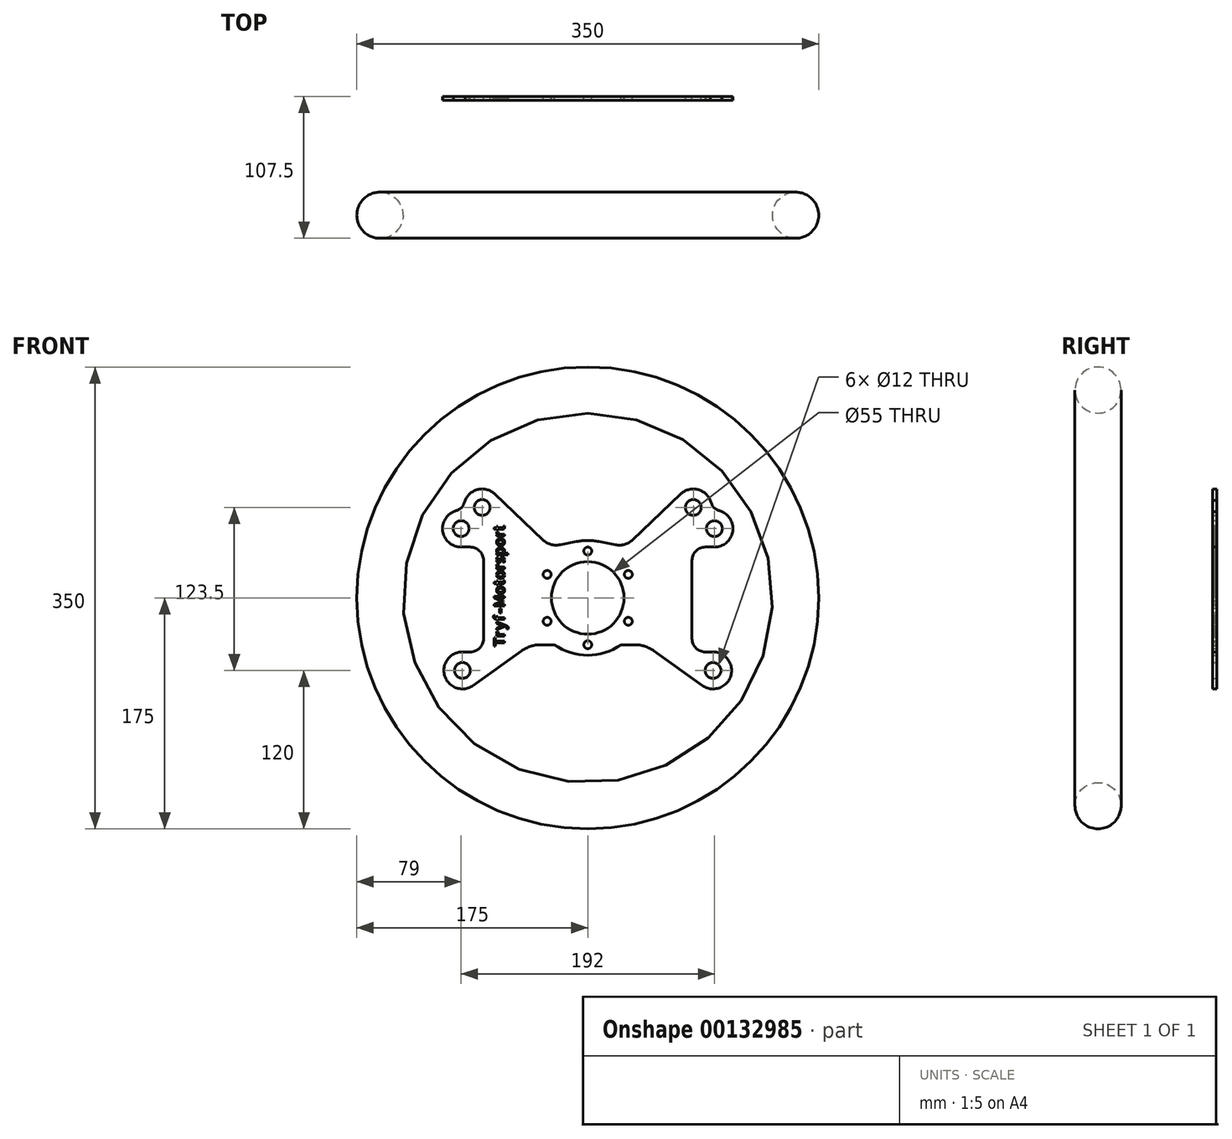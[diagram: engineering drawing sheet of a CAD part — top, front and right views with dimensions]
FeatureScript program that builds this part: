
annotation { "Feature Type Name" : "Feature", "Feature Type Description" : "" }
export const myFeature = defineFeature(function(context is Context, id is Id, definition is map)
    precondition{}
    {
        {
            var Q0;
            Q0=qCreatedBy(makeId("Front.planeOp"),FACE);
            cPlane(context, id + "F0", {"entities" : qUnion([Q0]), "cplaneType" : CPlaneType.OFFSET, "offset" : 90 * mm, "oppositeDirection" : true, "width" : 150 * mm, "height" : 150 * mm});
        }
        {
            var Q0;
            Q0=qCreatedBy(id+"F0.planeOp",FACE);
            var sketch = newSketch(context, id + "F1", { "sketchPlane" : qUnion([Q0])});
            skLineSegment(sketch, "E0", {"start": v(0, 175) * mm, "end": v(0, -175) * mm, "construction": true});
            skLineSegment(sketch, "E1", {"start": v(-175, 0) * mm, "end": v(175, 0) * mm, "construction": true});
            skCircle(sketch, "E2", {"center": v(0, 0) * mm, "radius": 175 * mm, "construction": true});
            skCircle(sketch, "E3", {"center": v(0, 0) * mm, "radius": 27.5 * mm});
            skCircle(sketch, "E4", {"center": v(0, 35.5) * mm, "radius": 3 * mm});
            skCircle(sketch, "E5.1.0", {"center": v(-30.74, 17.75) * mm, "radius": 3 * mm});
            skCircle(sketch, "E5.2.0", {"center": v(-30.74, -17.75) * mm, "radius": 3 * mm});
            skCircle(sketch, "E5.3.0", {"center": v(0, -35.5) * mm, "radius": 3 * mm});
            skCircle(sketch, "E5.4.0", {"center": v(30.74, -17.75) * mm, "radius": 3 * mm});
            skCircle(sketch, "E5.5.0", {"center": v(30.74, 17.75) * mm, "radius": 3 * mm});
            skArc(sketch, "E6", {"start": v(-25.14, -35.5) * mm, "mid": v(0, -43.5) * mm, "end": v(25.14, -35.5) * mm});
            skLineSegment(sketch, "E7", {"start": v(0, 68.5) * mm, "end": v(-80, 68.5) * mm, "construction": true});
            skCircle(sketch, "E8", {"center": v(-80, 68.5) * mm, "radius": 6 * mm});
            skCircle(sketch, "E9", {"center": v(-96, 52.5) * mm, "radius": 6 * mm});
            skCircle(sketch, "E10", {"center": v(-95, -55) * mm, "radius": 6 * mm});
            skArc(sketch, "E11.0", {"start": v(-101.8, 65.25) * mm, "mid": v(-109.68, 49.54) * mm, "end": v(-96, 38.5) * mm});
            skArc(sketch, "E12.0", {"start": v(-95, -41) * mm, "mid": v(-108.33, -59.27) * mm, "end": v(-86.87, -66.4) * mm});
            skLineSegment(sketch, "E13", {"start": v(-34.16, 44.1) * mm, "end": v(-70.33, 78.63) * mm});
            skLineSegment(sketch, "E14", {"start": v(-95, -41) * mm, "end": v(-89, -41) * mm});
            skLineSegment(sketch, "E15", {"start": v(-79, -31) * mm, "end": v(-79, 28.5) * mm});
            skLineSegment(sketch, "E16", {"start": v(-96, 38.5) * mm, "end": v(-89, 38.5) * mm});
            skPoint(sketch, "E17.visualSharp", {"position": v(-79, 38.5) * mm});
            skArc(sketch, "E17.filletArc", {"start": v(-79, 28.5) * mm, "mid": v(-81.93, 35.57) * mm, "end": v(-89, 38.5) * mm});
            skPoint(sketch, "E18.visualSharp", {"position": v(-79, -41) * mm});
            skArc(sketch, "E18.filletArc", {"start": v(-89, -41) * mm, "mid": v(-81.93, -38.07) * mm, "end": v(-79, -31) * mm});
            skArc(sketch, "E19.trimOffspring", {"start": v(-70.33, 78.63) * mm, "mid": v(-82.91, 82.2) * mm, "end": v(-92.95, 73.82) * mm});
            skLineSegment(sketch, "E20", {"start": v(-95.25, 67.75) * mm, "end": v(-82.17, 54.67) * mm, "construction": true});
            skLineSegment(sketch, "E21", {"start": v(-20.94, 40.24) * mm, "end": v(-8.32, 42.7) * mm});
            skPoint(sketch, "E22.newPointA", {"position": v(-24.45, 39.55) * mm});
            skPoint(sketch, "E22.newPointB", {"position": v(-25.14, 35.5) * mm});
            skArc(sketch, "E22.filletArc", {"start": v(-34.16, 44.1) * mm, "mid": v(-28.02, 40.57) * mm, "end": v(-20.94, 40.24) * mm});
            skPoint(sketch, "E23.orphan", {"position": v(-95, -69) * mm});
            skLineSegment(sketch, "E24.MirrorCS", {"start": v(20.94, 40.24) * mm, "end": v(8.32, 42.7) * mm});
            skArc(sketch, "E25.MirrorCS", {"start": v(34.16, 44.1) * mm, "mid": v(28.02, 40.57) * mm, "end": v(20.94, 40.24) * mm});
            skLineSegment(sketch, "E26.MirrorCS", {"start": v(34.16, 44.1) * mm, "end": v(70.33, 78.63) * mm});
            skArc(sketch, "E27.MirrorCS", {"start": v(70.33, 78.63) * mm, "mid": v(82.91, 82.2) * mm, "end": v(92.95, 73.82) * mm});
            skCircle(sketch, "E28.MirrorC", {"center": v(80, 68.5) * mm, "radius": 6 * mm});
            skArc(sketch, "E29.MirrorCS", {"start": v(101.8, 65.25) * mm, "mid": v(109.68, 49.54) * mm, "end": v(96, 38.5) * mm});
            skCircle(sketch, "E30.MirrorC", {"center": v(96, 52.5) * mm, "radius": 6 * mm});
            skLineSegment(sketch, "E31.MirrorCS", {"start": v(96, 38.5) * mm, "end": v(89, 38.5) * mm});
            skArc(sketch, "E32.MirrorCS", {"start": v(79, 28.5) * mm, "mid": v(81.93, 35.57) * mm, "end": v(89, 38.5) * mm});
            skLineSegment(sketch, "E33.MirrorCS", {"start": v(79, -31) * mm, "end": v(79, 28.5) * mm});
            skArc(sketch, "E34.MirrorCS", {"start": v(89, -41) * mm, "mid": v(81.93, -38.07) * mm, "end": v(79, -31) * mm});
            skLineSegment(sketch, "E35.MirrorCS", {"start": v(95, -41) * mm, "end": v(89, -41) * mm});
            skArc(sketch, "E36.MirrorCS", {"start": v(95, -41) * mm, "mid": v(108.33, -59.27) * mm, "end": v(86.87, -66.4) * mm});
            skLineSegment(sketch, "E37", {"start": v(-25.14, -35.5) * mm, "end": v(-35.53, -35.5) * mm});
            skLineSegment(sketch, "E38", {"start": v(-50.05, -40.14) * mm, "end": v(-86.87, -66.4) * mm});
            skPoint(sketch, "E39.visualSharp", {"position": v(-43.53, -35.5) * mm});
            skArc(sketch, "E39.filletArc", {"start": v(-35.53, -35.5) * mm, "mid": v(-43.15, -36.69) * mm, "end": v(-50.05, -40.14) * mm});
            skLineSegment(sketch, "E40.MirrorCS", {"start": v(50.05, -40.14) * mm, "end": v(86.87, -66.4) * mm});
            skArc(sketch, "E41.MirrorCS", {"start": v(35.53, -35.5) * mm, "mid": v(43.15, -36.69) * mm, "end": v(50.05, -40.14) * mm});
            skLineSegment(sketch, "E42.MirrorCS", {"start": v(25.14, -35.5) * mm, "end": v(35.53, -35.5) * mm});
            skCircle(sketch, "E43.MirrorC", {"center": v(95, -55) * mm, "radius": 6 * mm});
            skArc(sketch, "E44.trimOffspring", {"start": v(8.32, 42.7) * mm, "mid": v(0, 43.5) * mm, "end": v(-8.32, 42.7) * mm});
            skFitSpline(sketch, "E45", {"points": [v(-101.8, 65.25) * mm, v(-92.95, 73.82) * mm], "startDerivative": vector(19.64, 7.5) * mm, "endDerivative": vector(6.89, 18.23) * mm});
            skPoint(sketch, "E46.orphan", {"position": v(-93.83, 66.33) * mm});
            skFitSpline(sketch, "E47.MirrorCS", {"points": [v(101.8, 65.25) * mm, v(92.95, 73.82) * mm], "startDerivative": vector(-19.64, 7.5) * mm, "endDerivative": vector(-6.89, 18.23) * mm});
            skPoint(sketch, "E48.orphan", {"position": v(93.83, 66.33) * mm});
            skSolve(sketch);
        }
        {
            var Q0;
            Q0=makeQuery(id+"F1.imprint","IMPRINT",FACE,{"disambiguationData":[TD([[makeQuery(id+"F1.imprint","IMPRINT",EDGE,{"derivedFrom":sQuery(id+"F1.wireOp",EDGE,"E8")}),-1.0]])]});
            var Q1;
            Q1=makeQuery(id+"F1.imprint","IMPRINT",FACE,{"disambiguationData":[TD([[makeQuery(id+"F1.imprint","IMPRINT",EDGE,{"derivedFrom":sQuery(id+"F1.wireOp",EDGE,"E3")}),-1.0]])]});
            var Q2;
            {var subQ1=sQuery(id+"F1.wireOp",EDGE,"b0811fea-489b-4566-85c7-14dbea3367a90.MirrorCS");Q2=makeQuery(id+"F1.imprint","IMPRINT",FACE,{"disambiguationData":[TD([[makeQuery(id+"F1.imprint","IMPRINT",EDGE,{"derivedFrom":subQ1}),1.0]])]});}
            extrude(context, id + "F2", {"entities" : qUnion([Q0, Q1, Q2]), "depth" : 3 * mm});
        }
        {
            var Q0;
            Q0=makeQuery(id+"F2.opExtrude","SWEPT_BODY",BODY,{"disambiguationData":[OSD([sQuery(id+"F1.wireOp",EDGE,"E3"),sQuery(id+"F1.wireOp",EDGE,"E4"),sQuery(id+"F1.wireOp",EDGE,"E5.1.0"),sQuery(id+"F1.wireOp",EDGE,"E5.2.0"),sQuery(id+"F1.wireOp",EDGE,"E5.3.0"),sQuery(id+"F1.wireOp",EDGE,"E5.4.0"),sQuery(id+"F1.wireOp",EDGE,"E5.5.0"),sQuery(id+"F1.wireOp",EDGE,"E6"),sQuery(id+"F1.wireOp",EDGE,"E8"),sQuery(id+"F1.wireOp",EDGE,"E9"),sQuery(id+"F1.wireOp",EDGE,"E10"),sQuery(id+"F1.wireOp",EDGE,"E11.0"),sQuery(id+"F1.wireOp",EDGE,"E12.0"),sQuery(id+"F1.wireOp",EDGE,"E13"),sQuery(id+"F1.wireOp",EDGE,"E14"),sQuery(id+"F1.wireOp",EDGE,"E15"),sQuery(id+"F1.wireOp",EDGE,"E16"),sQuery(id+"F1.wireOp",EDGE,"E17.filletArc"),sQuery(id+"F1.wireOp",EDGE,"E18.filletArc"),sQuery(id+"F1.wireOp",EDGE,"E19.trimOffspring"),sQuery(id+"F1.wireOp",EDGE,"E21"),sQuery(id+"F1.wireOp",EDGE,"E22.filletArc"),sQuery(id+"F1.wireOp",EDGE,"E24.MirrorCS"),sQuery(id+"F1.wireOp",EDGE,"E25.MirrorCS"),sQuery(id+"F1.wireOp",EDGE,"E26.MirrorCS"),sQuery(id+"F1.wireOp",EDGE,"E27.MirrorCS"),sQuery(id+"F1.wireOp",EDGE,"E28.MirrorC"),sQuery(id+"F1.wireOp",EDGE,"E29.MirrorCS"),sQuery(id+"F1.wireOp",EDGE,"E30.MirrorC"),sQuery(id+"F1.wireOp",EDGE,"E31.MirrorCS"),sQuery(id+"F1.wireOp",EDGE,"E32.MirrorCS"),sQuery(id+"F1.wireOp",EDGE,"E33.MirrorCS"),sQuery(id+"F1.wireOp",EDGE,"E34.MirrorCS"),sQuery(id+"F1.wireOp",EDGE,"E35.MirrorCS"),sQuery(id+"F1.wireOp",EDGE,"E36.MirrorCS"),sQuery(id+"F1.wireOp",EDGE,"E37"),sQuery(id+"F1.wireOp",EDGE,"E38"),sQuery(id+"F1.wireOp",EDGE,"E39.filletArc"),sQuery(id+"F1.wireOp",EDGE,"E40.MirrorCS"),sQuery(id+"F1.wireOp",EDGE,"E41.MirrorCS"),sQuery(id+"F1.wireOp",EDGE,"E42.MirrorCS"),sQuery(id+"F1.wireOp",EDGE,"E43.MirrorC"),sQuery(id+"F1.wireOp",EDGE,"E44.trimOffspring"),sQuery(id+"F1.wireOp",EDGE,"E45"),sQuery(id+"F1.wireOp",EDGE,"E47.MirrorCS")])]});
            var Q1;
            Q1=makeQuery(id+"F2.opExtrude","CAP_EDGE",EDGE,{"disambiguationData":[OSD([sQuery(id+"F1.wireOp",EDGE,"E3")])],"isStart":false});
            transform(context, id + "F3", {"entities" : qUnion([Q0]), "transformType" : TransformType.ROTATION, "transformAxis" : qUnion([Q1]), "angle" : 90 * degree, "oppositeDirection" : true, "makeCopy" : false});
        }
        {
            var Q0;
            Q0=makeQuery(id+"F2.opExtrude","CAP_FACE",FACE,{"disambiguationData":[OSD([sQuery(id+"F1.wireOp",EDGE,"E3"),sQuery(id+"F1.wireOp",EDGE,"E4"),sQuery(id+"F1.wireOp",EDGE,"E5.1.0"),sQuery(id+"F1.wireOp",EDGE,"E5.2.0"),sQuery(id+"F1.wireOp",EDGE,"E5.3.0"),sQuery(id+"F1.wireOp",EDGE,"E5.4.0"),sQuery(id+"F1.wireOp",EDGE,"E5.5.0"),sQuery(id+"F1.wireOp",EDGE,"E6"),sQuery(id+"F1.wireOp",EDGE,"E8"),sQuery(id+"F1.wireOp",EDGE,"E9"),sQuery(id+"F1.wireOp",EDGE,"E10"),sQuery(id+"F1.wireOp",EDGE,"E11.0"),sQuery(id+"F1.wireOp",EDGE,"E12.0"),sQuery(id+"F1.wireOp",EDGE,"E13"),sQuery(id+"F1.wireOp",EDGE,"E14"),sQuery(id+"F1.wireOp",EDGE,"E15"),sQuery(id+"F1.wireOp",EDGE,"E16"),sQuery(id+"F1.wireOp",EDGE,"E17.filletArc"),sQuery(id+"F1.wireOp",EDGE,"E18.filletArc"),sQuery(id+"F1.wireOp",EDGE,"E19.trimOffspring"),sQuery(id+"F1.wireOp",EDGE,"E21"),sQuery(id+"F1.wireOp",EDGE,"E22.filletArc"),sQuery(id+"F1.wireOp",EDGE,"E24.MirrorCS"),sQuery(id+"F1.wireOp",EDGE,"E25.MirrorCS"),sQuery(id+"F1.wireOp",EDGE,"E26.MirrorCS"),sQuery(id+"F1.wireOp",EDGE,"E27.MirrorCS"),sQuery(id+"F1.wireOp",EDGE,"E28.MirrorC"),sQuery(id+"F1.wireOp",EDGE,"E29.MirrorCS"),sQuery(id+"F1.wireOp",EDGE,"E30.MirrorC"),sQuery(id+"F1.wireOp",EDGE,"E31.MirrorCS"),sQuery(id+"F1.wireOp",EDGE,"E32.MirrorCS"),sQuery(id+"F1.wireOp",EDGE,"E33.MirrorCS"),sQuery(id+"F1.wireOp",EDGE,"E34.MirrorCS"),sQuery(id+"F1.wireOp",EDGE,"E35.MirrorCS"),sQuery(id+"F1.wireOp",EDGE,"E36.MirrorCS"),sQuery(id+"F1.wireOp",EDGE,"E37"),sQuery(id+"F1.wireOp",EDGE,"E38"),sQuery(id+"F1.wireOp",EDGE,"E39.filletArc"),sQuery(id+"F1.wireOp",EDGE,"E40.MirrorCS"),sQuery(id+"F1.wireOp",EDGE,"E41.MirrorCS"),sQuery(id+"F1.wireOp",EDGE,"E42.MirrorCS"),sQuery(id+"F1.wireOp",EDGE,"E43.MirrorC"),sQuery(id+"F1.wireOp",EDGE,"E44.trimOffspring"),sQuery(id+"F1.wireOp",EDGE,"E45"),sQuery(id+"F1.wireOp",EDGE,"E47.MirrorCS")])],"isStart":false});
            var sketch = newSketch(context, id + "F4", { "sketchPlane" : qUnion([Q0])});
            skText(sketch, "E49", { "text": "Tryf-Motorsport", "fontName": "AllertaStencil-Regular.ttf"});
            const initialGuessF4  = {"E49": [-0.037, 0.063, 1, 0, 0.008]};
            skSetInitialGuess(sketch, initialGuessF4);
            skSolve(sketch);
        }
        {
            var Q0;
            Q0 = qSketchRegion(id + "F4", true);
            extrude(context, id + "F5", {"entities" : qUnion([Q0]), "operationType" : NewBodyOperationType.REMOVE, "oppositeDirection" : true, "depth" : 5 * mm, "hasSecondDirection" : true, "secondDirectionOppositeDirection" : false, "secondDirectionDepth" : 5 * mm});
        }
        {
            var Q0;
            Q0=makeQuery(id+"F2.opExtrude","SWEPT_BODY",BODY,{"disambiguationData":[OSD([sQuery(id+"F1.wireOp",EDGE,"E3"),sQuery(id+"F1.wireOp",EDGE,"E4"),sQuery(id+"F1.wireOp",EDGE,"E5.1.0"),sQuery(id+"F1.wireOp",EDGE,"E5.2.0"),sQuery(id+"F1.wireOp",EDGE,"E5.3.0"),sQuery(id+"F1.wireOp",EDGE,"E5.4.0"),sQuery(id+"F1.wireOp",EDGE,"E5.5.0"),sQuery(id+"F1.wireOp",EDGE,"E6"),sQuery(id+"F1.wireOp",EDGE,"E8"),sQuery(id+"F1.wireOp",EDGE,"E9"),sQuery(id+"F1.wireOp",EDGE,"E10"),sQuery(id+"F1.wireOp",EDGE,"E11.0"),sQuery(id+"F1.wireOp",EDGE,"E12.0"),sQuery(id+"F1.wireOp",EDGE,"E13"),sQuery(id+"F1.wireOp",EDGE,"E14"),sQuery(id+"F1.wireOp",EDGE,"E15"),sQuery(id+"F1.wireOp",EDGE,"E16"),sQuery(id+"F1.wireOp",EDGE,"E17.filletArc"),sQuery(id+"F1.wireOp",EDGE,"E18.filletArc"),sQuery(id+"F1.wireOp",EDGE,"E19.trimOffspring"),sQuery(id+"F1.wireOp",EDGE,"E21"),sQuery(id+"F1.wireOp",EDGE,"E22.filletArc"),sQuery(id+"F1.wireOp",EDGE,"E24.MirrorCS"),sQuery(id+"F1.wireOp",EDGE,"E25.MirrorCS"),sQuery(id+"F1.wireOp",EDGE,"E26.MirrorCS"),sQuery(id+"F1.wireOp",EDGE,"E27.MirrorCS"),sQuery(id+"F1.wireOp",EDGE,"E28.MirrorC"),sQuery(id+"F1.wireOp",EDGE,"E29.MirrorCS"),sQuery(id+"F1.wireOp",EDGE,"E30.MirrorC"),sQuery(id+"F1.wireOp",EDGE,"E31.MirrorCS"),sQuery(id+"F1.wireOp",EDGE,"E32.MirrorCS"),sQuery(id+"F1.wireOp",EDGE,"E33.MirrorCS"),sQuery(id+"F1.wireOp",EDGE,"E34.MirrorCS"),sQuery(id+"F1.wireOp",EDGE,"E35.MirrorCS"),sQuery(id+"F1.wireOp",EDGE,"E36.MirrorCS"),sQuery(id+"F1.wireOp",EDGE,"E37"),sQuery(id+"F1.wireOp",EDGE,"E38"),sQuery(id+"F1.wireOp",EDGE,"E39.filletArc"),sQuery(id+"F1.wireOp",EDGE,"E40.MirrorCS"),sQuery(id+"F1.wireOp",EDGE,"E41.MirrorCS"),sQuery(id+"F1.wireOp",EDGE,"E42.MirrorCS"),sQuery(id+"F1.wireOp",EDGE,"E43.MirrorC"),sQuery(id+"F1.wireOp",EDGE,"E44.trimOffspring"),sQuery(id+"F1.wireOp",EDGE,"E45"),sQuery(id+"F1.wireOp",EDGE,"E47.MirrorCS")])]});
            var Q1;
            Q1=makeQuery(id+"F2.opExtrude","CAP_EDGE",EDGE,{"disambiguationData":[OSD([sQuery(id+"F1.wireOp",EDGE,"E3")])],"isStart":false});
            transform(context, id + "F6", {"entities" : qUnion([Q0]), "transformType" : TransformType.ROTATION, "transformAxis" : qUnion([Q1]), "angle" : 90 * degree, "makeCopy" : false});
        }
        {
            var Q0;
            Q0=sQuery(id+"F1.wireOp",VERTEX,"E0.start");
            var Q1;
            Q1=sQuery(id+"F1.wireOp",EDGE,"E2");
            cPlane(context, id + "F7", {"entities" : qUnion([Q0, Q1]), "cplaneType" : CPlaneType.CURVE_POINT, "offset" : 25 * mm, "width" : 150 * mm, "height" : 150 * mm});
        }
        {
            var Q0;
            Q0=qCreatedBy(id+"F7.planeOp",FACE);
            var sketch = newSketch(context, id + "F8", { "sketchPlane" : qUnion([Q0])});
            skCircle(sketch, "E50", {"center": v(0, 157.5) * mm, "radius": 17.5 * mm});
            skSolve(sketch);
        }
        {
            var Q0;
            Q0 = qSketchRegion(id + "F8", true);
            var Q1;
            Q1=sQuery(id+"F1.wireOp",EDGE,"E2");
            revolve(context, id + "F9", {"entities" : qUnion([Q0]), "axis" : qUnion([Q1]), "revolveType" : RevolveType.FULL});
        }
    });
